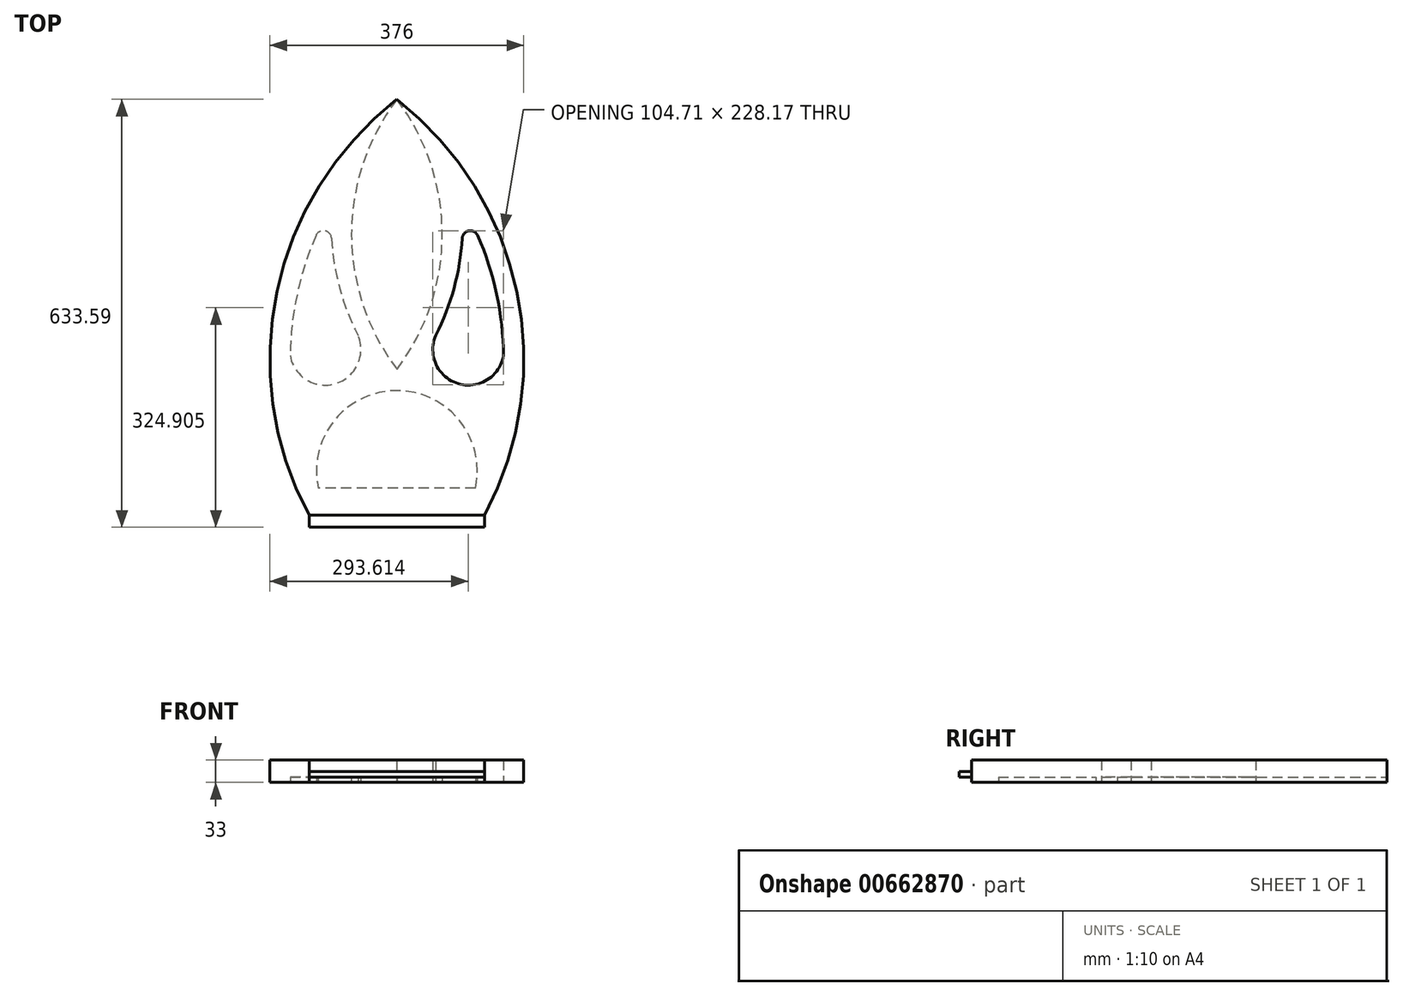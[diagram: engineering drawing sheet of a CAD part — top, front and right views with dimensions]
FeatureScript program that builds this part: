
annotation { "Feature Type Name" : "Feature", "Feature Type Description" : "" }
export const myFeature = defineFeature(function(context is Context, id is Id, definition is map)
    precondition{}
    {
        {
            var Q0;
            Q0=qCreatedBy(makeId("Top.planeOp"),FACE);
            var sketch = newSketch(context, id + "F0", { "sketchPlane" : qUnion([Q0])});
            skLineSegment(sketch, "E0", {"start": v(0, -400) * mm, "end": v(-200, -400) * mm});
            skLineSegment(sketch, "E1", {"start": v(200, -400) * mm, "end": v(0, -400) * mm});
            skArc(sketch, "E2", {"start": v(0, 400) * mm, "mid": v(-189.7, 100.97) * mm, "end": v(-133.76, -248.7) * mm});
            skArc(sketch, "E3", {"start": v(133.76, -248.7) * mm, "mid": v(189.7, 100.97) * mm, "end": v(0, 400) * mm});
            skArc(sketch, "E4", {"start": v(-0.29, 384.51) * mm, "mid": v(-67.25, 184.58) * mm, "end": v(0.28, -15.16) * mm});
            skArc(sketch, "E5.MirrorCS", {"start": v(0.29, 384.51) * mm, "mid": v(67.37, 184.66) * mm, "end": v(0, -15.1) * mm});
            skLineSegment(sketch, "E6", {"start": v(133.76, -248.7) * mm, "end": v(-133.76, -248.7) * mm});
            skArc(sketch, "E7.0", {"start": v(7.2, 390.4) * mm, "mid": v(7.14, 390.36) * mm, "end": v(7.09, 390.32) * mm});
            skArc(sketch, "E8.MirrorCS", {"start": v(-7.2, 390.4) * mm, "mid": v(-7.14, 390.36) * mm, "end": v(-7.09, 390.32) * mm});
            skArc(sketch, "E9.0", {"start": v(0, 364.37) * mm, "mid": v(55.37, 184.9) * mm, "end": v(0, 5.42) * mm});
            skArc(sketch, "E9.1", {"start": v(0, 364.37) * mm, "mid": v(-55.37, 184.9) * mm, "end": v(0, 5.42) * mm});
            skArc(sketch, "E10.trimOffspring", {"start": v(0, 384.9) * mm, "mid": v(-177.47, 100.85) * mm, "end": v(-130.02, -230.7) * mm});
            skArc(sketch, "E11.trimOffspring", {"start": v(0, 384.9) * mm, "mid": v(177.47, 100.85) * mm, "end": v(130.02, -230.7) * mm});
            skArc(sketch, "E12.0", {"start": v(-119.75, 183.24) * mm, "mid": v(-147.78, 96.23) * mm, "end": v(-157.97, 5.38) * mm});
            skArc(sketch, "E13.0", {"start": v(-96.77, 179.13) * mm, "mid": v(-84.7, 105.25) * mm, "end": v(-57.64, 35.46) * mm});
            skPoint(sketch, "E14.orphan", {"position": v(0, -248.7) * mm});
            skLineSegment(sketch, "E15.0", {"start": v(130.02, -230.7) * mm, "end": v(-130.02, -230.7) * mm});
            skArc(sketch, "E16.MirrorCS", {"start": v(96.77, 179.13) * mm, "mid": v(84.7, 105.25) * mm, "end": v(57.64, 35.46) * mm});
            skArc(sketch, "E17.MirrorCS", {"start": v(119.75, 183.24) * mm, "mid": v(147.78, 96.23) * mm, "end": v(157.97, 5.38) * mm});
            skArc(sketch, "E18", {"start": v(116.4, -190.7) * mm, "mid": v(0, -46.44) * mm, "end": v(-116.4, -190.7) * mm});
            skPoint(sketch, "E19.visualSharp", {"position": v(-96.13, 229.87) * mm});
            skArc(sketch, "E19.filletArc", {"start": v(-96.77, 179.13) * mm, "mid": v(-106.64, 190.25) * mm, "end": v(-119.75, 183.24) * mm});
            skPoint(sketch, "E20.visualSharp", {"position": v(96.13, 229.87) * mm});
            skArc(sketch, "E20.filletArc", {"start": v(119.75, 183.24) * mm, "mid": v(106.64, 190.25) * mm, "end": v(96.77, 179.13) * mm});
            skPoint(sketch, "E21.orphan", {"position": v(0, -46.44) * mm});
            skLineSegment(sketch, "E22.trimOffspring", {"start": v(116.4, -190.7) * mm, "end": v(-116.4, -190.7) * mm});
            skPoint(sketch, "E23.orphan", {"position": v(-200, -248.7) * mm});
            skPoint(sketch, "E24.orphan", {"position": v(200, -248.7) * mm});
            skLineSegment(sketch, "E25", {"start": v(-130.02, -230.7) * mm, "end": v(-130.02, -248.7) * mm});
            skLineSegment(sketch, "E26", {"start": v(130.02, -230.7) * mm, "end": v(130.02, -248.7) * mm});
            skArc(sketch, "E27", {"start": v(-157.97, 5.38) * mm, "mid": v(-90.86, -36.11) * mm, "end": v(-57.64, 35.46) * mm});
            skArc(sketch, "E28.MirrorCS", {"start": v(157.97, 5.38) * mm, "mid": v(90.86, -36.11) * mm, "end": v(57.64, 35.46) * mm});
            skLineSegment(sketch, "E29", {"start": v(0, 400) * mm, "end": v(0, 384.9) * mm});
            skPoint(sketch, "E30.startSnap0", {"position": v(-67.25, 184.82) * mm});
            skLineSegment(sketch, "E31", {"start": v(-0.29, 384.51) * mm, "end": v(0.29, 384.51) * mm});
            skLineSegment(sketch, "E32", {"start": v(-271.82, -248.7) * mm, "end": v(-263.78, 400) * mm});
            skPoint(sketch, "E33.orphan", {"position": v(-263.17, 449.61) * mm});
            skSolve(sketch);
        }
        {
            var Q0;
            Q0=makeQuery(id+"F0.imprint","IMPRINT",FACE,{"disambiguationData":[TD([[makeQuery(id+"F0.imprint","IMPRINT",EDGE,{"derivedFrom":sQuery(id+"F0.wireOp",EDGE,"E10.trimOffspring")}),1.0]])]});
            extrude(context, id + "F1", {"entities" : qUnion([Q0]), "endBound" : BoundingType.SYMMETRIC, "depth" : 16 * mm, "offsetDistance" : 25 * mm});
        }
        {
            var Q0;
            Q0=makeQuery(id+"F0.imprint","IMPRINT",FACE,{"disambiguationData":[TD([[makeQuery(id+"F0.imprint","IMPRINT",EDGE,{"derivedFrom":sQuery(id+"F0.wireOp",EDGE,"E10.trimOffspring")}),1.0]])]});
            var Q1;
            Q1=makeQuery(id+"F0.imprint","IMPRINT",FACE,{"disambiguationData":[TD([[makeQuery(id+"F0.imprint","IMPRINT",EDGE,{"derivedFrom":sQuery(id+"F0.wireOp",EDGE,"E18")}),1.0]])]});
            var Q2;
            Q2=makeQuery(id+"F0.imprint","IMPRINT",FACE,{"disambiguationData":[TD([[makeQuery(id+"F0.imprint","IMPRINT",EDGE,{"derivedFrom":sQuery(id+"F0.wireOp",EDGE,"E12.0")}),1.0]])]});
            var Q3;
            Q3=makeQuery(id+"F0.imprint","IMPRINT",FACE,{"disambiguationData":[TD([[makeQuery(id+"F0.imprint","IMPRINT",EDGE,{"derivedFrom":sQuery(id+"F0.wireOp",EDGE,"E9.0")}),1.0]])]});
            var Q4;
            Q4=makeQuery(id+"F0.imprint","IMPRINT",FACE,{"disambiguationData":[TD([[makeQuery(id+"F0.imprint","IMPRINT",EDGE,{"derivedFrom":sQuery(id+"F0.wireOp",EDGE,"E9.0")}),-1.0]])]});
            var Q5;
            Q5=makeQuery(id+"F0.imprint","IMPRINT",FACE,{"disambiguationData":[TD([[makeQuery(id+"F0.imprint","IMPRINT",EDGE,{"derivedFrom":sQuery(id+"F0.wireOp",EDGE,"E16.MirrorCS")}),1.0]])]});
            extrude(context, id + "F2", {"entities" : qUnion([Q0, Q1, Q2, Q3, Q4, Q5]), "depth" : 25 * mm, "offsetDistance" : 25 * mm});
        }
        {
            var Q0;
            Q0=makeQuery(id+"F0.imprint","IMPRINT",FACE,{"disambiguationData":[TD([[makeQuery(id+"F0.imprint","IMPRINT",EDGE,{"derivedFrom":sQuery(id+"F0.wireOp",EDGE,"E15.0")}),1.0]])]});
            extrude(context, id + "F3", {"entities" : qUnion([Q0]), "operationType" : NewBodyOperationType.ADD, "depth" : 8 * mm, "offsetDistance" : 25 * mm});
        }
    });
